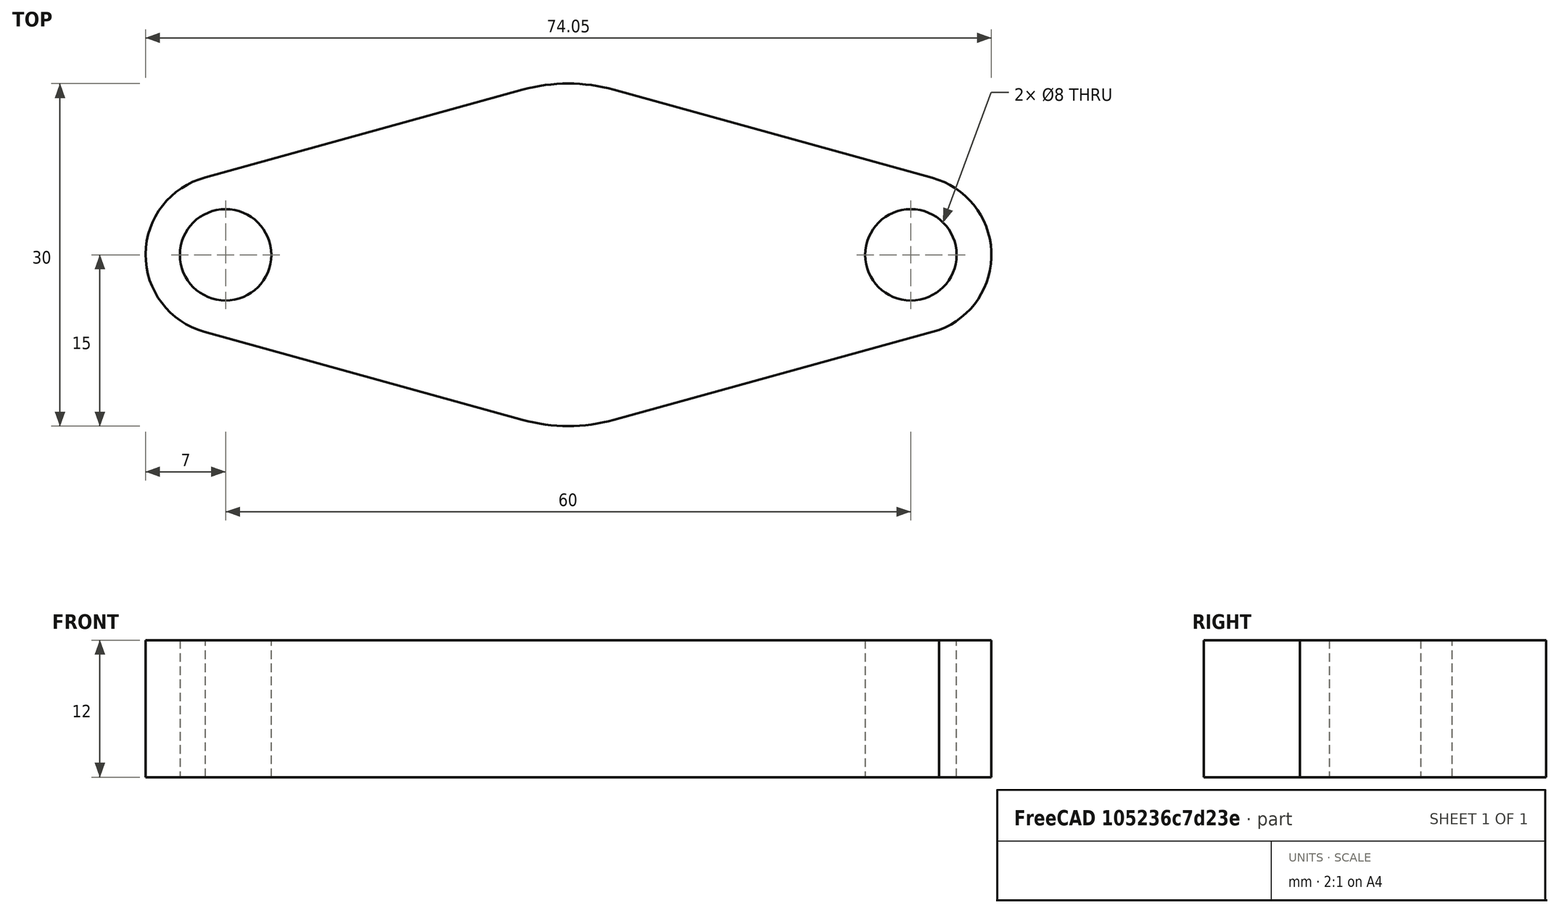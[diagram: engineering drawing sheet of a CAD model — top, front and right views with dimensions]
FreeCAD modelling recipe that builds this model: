
FCSTD DOCUMENT  (FreeCAD 0.19R24267 +148 (Git))
Label: Yataklı Rulman
License: All rights reserved
LicenseURL: http://en.wikipedia.org/wiki/All_rights_reserved
objects: Sketcher::SketchObject×2, PartDesign::Pad×1, PartDesign::Body×1
note: 5 computed .brp shape members not serialized (recipe doc carries the construction recipe); baked Part::Feature solids carry a one-line shape summary decoded from their .brp

FEATURE [Sketcher::SketchObject] Sketch
  FullyConstrained = false
  MapMode = 5
  Support = -> [XY_Plane]
  sketch-geometry (10):
    g0: ArcOfCircle CenterX=0 CenterY=0 CenterZ=0 NormalX=0 NormalY=0 NormalZ=1 AngleXU=0 Radius=15 StartAngle=4.44246 EndAngle=4.98232
    g1: Circle CenterX=-30 CenterY=0 CenterZ=0 NormalX=0 NormalY=0 NormalZ=1 AngleXU=0 Radius=4
    g2: Circle CenterX=30 CenterY=0 CenterZ=0 NormalX=0 NormalY=0 NormalZ=1 AngleXU=0 Radius=4
    g3: ArcOfCircle CenterX=-30 CenterY=0 CenterZ=0 NormalX=0 NormalY=0 NormalZ=1 AngleXU=0 Radius=7 StartAngle=1.82446 EndAngle=4.44246
    g4: LineSegment StartX=-31.7567 StartY=6.77599 StartZ=0 EndX=-4 EndY=14.4568 EndZ=0
    g5: LineSegment StartX=-31.8667 StartY=-6.74652 StartZ=0 EndX=-4 EndY=-14.4568 EndZ=0
    g6: ArcOfCircle CenterX=30.0474 CenterY=-0.012942 CenterZ=0 NormalX=0 NormalY=0 NormalZ=1 AngleXU=0 Radius=7 StartAngle=5.06705 EndAngle=7.59089
    g7: LineSegment StartX=32.4783 StartY=-6.57729 StartZ=0 EndX=4 EndY=-14.4568 EndZ=0
    g8: LineSegment StartX=31.8678 StartY=6.7462 StartZ=0 EndX=4 EndY=14.4568 EndZ=0
    g9: ArcOfCircle CenterX=0 CenterY=0 CenterZ=0 NormalX=0 NormalY=0 NormalZ=1 AngleXU=0 Radius=15 StartAngle=1.30086 EndAngle=1.84073
  constraints (24):
    c: Coincident(g0,g-1)
    c: PointOnObject(g1,g-1)
    c: PointOnObject(g2,g-1)
    c: DistanceX(g1,g0) = 30
    c: DistanceX(g0,g2) = 30
    c: Radius(g1) = 4
    c: Radius(g2) = 4
    c: Radius(g0) = 15
    c: Coincident(g3,g1)
    c: Coincident(g4,g3)
    c: Coincident(g5,g3)
    c: DistanceX(g5,g0) = 4
    c: DistanceX(g4,g0) = 4
    c: Tangent(g0,g5) = -1.5708
    c: Coincident(g9,g4) = 1.5708
    c: Coincident(g8,g6)
    c: Coincident(g7,g6)
    c: Radius(g6) = 7
    c: DistanceX(g0,g8) = 4
    c: Equal(g0,g9)
    c: Tangent(g0,g7) = 1.5708
    c: Tangent(g9,g8) = -1.5708
    c: Coincident(g0,g9)
    c: DistanceX(g0,g0) = 4
FEATURE [PartDesign::Pad] Pad
  Direction = (1,1,1)
  Length = 12
  Length2 = 100
  Profile = -> Sketch
  Type = 0
FEATURE [Sketcher::SketchObject] Sketch001
  FullyConstrained = false
  MapMode = 5
  Placement = pos=(0,0,0) rot=(1,0,0;1.5708rad)
  Support = -> [XZ_Plane]
  sketch-geometry (1):
    g0: LineSegment StartX=-40.1163 StartY=4 StartZ=0 EndX=-4.09868 EndY=16 EndZ=0
  constraints (2):
    c: DistanceY(g-1,g0) = 4
    c: DistanceY(g-1,g0) = 16
FEATURE [PartDesign::Body] Body
  Group = -> [Sketch,Pad,Sketch001]
  Origin = -> Origin
  Tip = -> Pad
